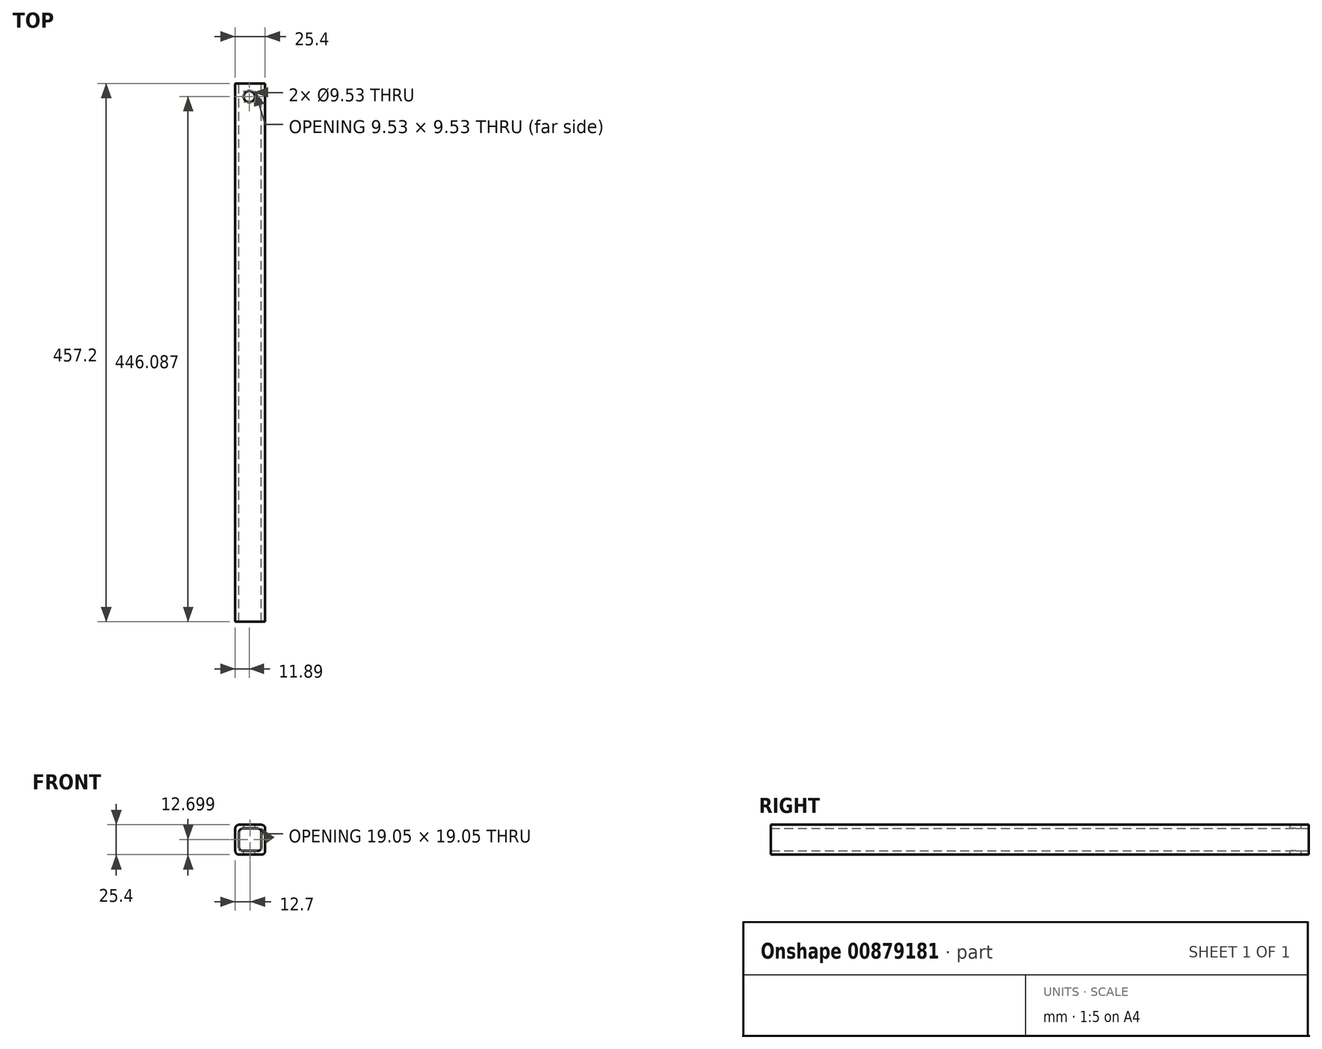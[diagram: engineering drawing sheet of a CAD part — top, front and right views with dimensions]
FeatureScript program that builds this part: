
annotation { "Feature Type Name" : "Feature", "Feature Type Description" : "" }
export const myFeature = defineFeature(function(context is Context, id is Id, definition is map)
    precondition{}
    {
        {
            var Q0;
            Q0=qCreatedBy(makeId("Front.planeOp"),FACE);
            var sketch = newSketch(context, id + "F0", { "sketchPlane" : qUnion([Q0])});
            skLineSegment(sketch, "E0.bottom", {"start": v(10.33, -12.26) * mm, "end": v(-8.72, -12.26) * mm});
            skLineSegment(sketch, "E0.top", {"start": v(10.33, 13.14) * mm, "end": v(-8.72, 13.14) * mm});
            skLineSegment(sketch, "E0.left", {"start": v(13.5, -9.09) * mm, "end": v(13.5, 9.96) * mm});
            skLineSegment(sketch, "E0.right", {"start": v(-11.9, -9.09) * mm, "end": v(-11.9, 9.96) * mm});
            skLineSegment(sketch, "E1.bottom", {"start": v(7.16, -9.09) * mm, "end": v(-5.54, -9.09) * mm});
            skLineSegment(sketch, "E1.top", {"start": v(7.16, 9.96) * mm, "end": v(-5.54, 9.96) * mm});
            skLineSegment(sketch, "E1.left", {"start": v(10.33, -5.91) * mm, "end": v(10.33, 6.79) * mm});
            skLineSegment(sketch, "E1.right", {"start": v(-8.72, -5.91) * mm, "end": v(-8.72, 6.79) * mm});
            skPoint(sketch, "E2.visualSharp", {"position": v(10.33, 9.96) * mm});
            skArc(sketch, "E2.filletArc", {"start": v(10.33, 6.79) * mm, "mid": v(9.4, 9.03) * mm, "end": v(7.16, 9.96) * mm});
            skPoint(sketch, "E3.visualSharp", {"position": v(-8.72, 9.96) * mm});
            skArc(sketch, "E3.filletArc", {"start": v(-5.54, 9.96) * mm, "mid": v(-7.79, 9.03) * mm, "end": v(-8.72, 6.79) * mm});
            skPoint(sketch, "E4.visualSharp", {"position": v(-8.72, -9.09) * mm});
            skArc(sketch, "E4.filletArc", {"start": v(-8.72, -5.91) * mm, "mid": v(-7.79, -8.16) * mm, "end": v(-5.54, -9.09) * mm});
            skPoint(sketch, "E5.visualSharp", {"position": v(10.33, -9.09) * mm});
            skArc(sketch, "E5.filletArc", {"start": v(7.16, -9.09) * mm, "mid": v(9.4, -8.16) * mm, "end": v(10.33, -5.91) * mm});
            skPoint(sketch, "E6.visualSharp", {"position": v(13.5, 13.14) * mm});
            skArc(sketch, "E6.filletArc", {"start": v(13.5, 9.96) * mm, "mid": v(12.58, 12.2) * mm, "end": v(10.33, 13.14) * mm});
            skPoint(sketch, "E7.visualSharp", {"position": v(-11.9, 13.14) * mm});
            skArc(sketch, "E7.filletArc", {"start": v(-8.72, 13.14) * mm, "mid": v(-10.96, 12.2) * mm, "end": v(-11.9, 9.96) * mm});
            skPoint(sketch, "E8.visualSharp", {"position": v(-11.9, -12.26) * mm});
            skArc(sketch, "E8.filletArc", {"start": v(-11.9, -9.09) * mm, "mid": v(-10.96, -11.33) * mm, "end": v(-8.72, -12.26) * mm});
            skPoint(sketch, "E9.visualSharp", {"position": v(13.5, -12.26) * mm});
            skArc(sketch, "E9.filletArc", {"start": v(10.33, -12.26) * mm, "mid": v(12.58, -11.33) * mm, "end": v(13.5, -9.09) * mm});
            skSolve(sketch);
        }
        {
            var Q0;
            Q0=qSketchRegion(id+"F0",true);
            extrude(context, id + "F1", {"entities" : qUnion([Q0]), "depth" : 457.2 * mm, "offsetDistance" : 25.4 * mm});
        }
        {
            var Q0;
            Q0=makeQuery(id+"F1.opExtrude","SWEPT_FACE",FACE,{"disambiguationData":[OSD([sQuery(id+"F0.wireOp",EDGE,"E0.top")])]});
            var sketch = newSketch(context, id + "F2", { "sketchPlane" : qUnion([Q0])});
            skCircle(sketch, "E10", {"center": v(0, -11.11) * mm, "radius": 4.76 * mm});
            skSolve(sketch);
        }
        {
            var Q0;
            Q0=makeQuery(id+"F2.imprint","IMPRINT",FACE,{"disambiguationData":[TD([[makeQuery(id+"F2.imprint","IMPRINT",EDGE,{"derivedFrom":sQuery(id+"F2.wireOp",EDGE,"E10")}),1.0]])]});
            extrude(context, id + "F3", {"entities" : qUnion([Q0]), "operationType" : NewBodyOperationType.REMOVE, "oppositeDirection" : true, "depth" : 25.4 * mm, "offsetDistance" : 25.4 * mm});
        }
    });
